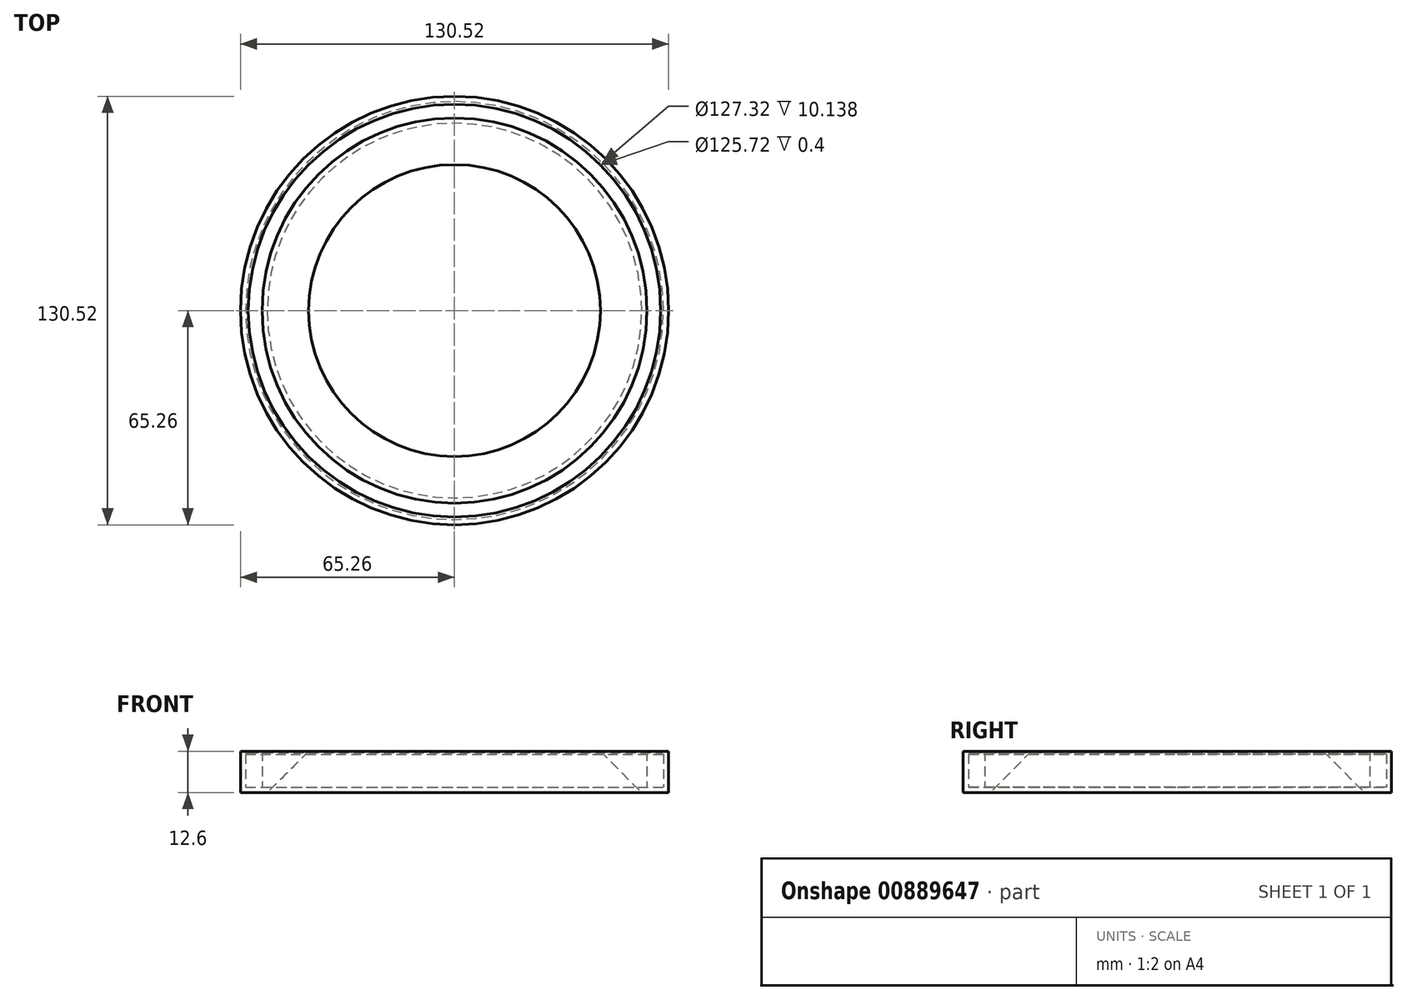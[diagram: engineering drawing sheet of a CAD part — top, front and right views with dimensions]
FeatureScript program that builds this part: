
annotation { "Feature Type Name" : "Feature", "Feature Type Description" : "" }
export const myFeature = defineFeature(function(context is Context, id is Id, definition is map)
    precondition{}
    {
        {
            var Q0;
            Q0=qCreatedBy(makeId("Front.planeOp"),FACE);
            var sketch = newSketch(context, id + "F0", { "sketchPlane" : qUnion([Q0])});
            skLineSegment(sketch, "E0", {"start": v(-65.26, 12.6) * mm, "end": v(-65.26, 0) * mm});
            skLineSegment(sketch, "E1", {"start": v(-65.26, 0) * mm, "end": v(-57.06, 0) * mm});
            skLineSegment(sketch, "E2", {"start": v(-57.06, 0) * mm, "end": v(-44.46, 12.6) * mm});
            skLineSegment(sketch, "E3", {"start": v(-44.46, 12.6) * mm, "end": v(-57.06, 12.6) * mm});
            skLineSegment(sketch, "E4", {"start": v(-57.06, 12.6) * mm, "end": v(-58.66, 12.6) * mm});
            skLineSegment(sketch, "E5", {"start": v(-58.66, 12.6) * mm, "end": v(-58.66, 1.6) * mm});
            skLineSegment(sketch, "E6", {"start": v(-58.66, 1.6) * mm, "end": v(-63.66, 1.6) * mm});
            skLineSegment(sketch, "E7", {"start": v(-63.66, 1.6) * mm, "end": v(-63.66, 12.6) * mm});
            skLineSegment(sketch, "E8", {"start": v(-63.66, 12.6) * mm, "end": v(-65.26, 12.6) * mm});
            skLineSegment(sketch, "E9", {"start": v(-63.66, 12.6) * mm, "end": v(-62.86, 12.6) * mm});
            skLineSegment(sketch, "E10", {"start": v(-62.86, 12.6) * mm, "end": v(-62.86, 12.2) * mm});
            skLineSegment(sketch, "E11", {"start": v(-62.86, 12.2) * mm, "end": v(-63.66, 11.74) * mm});
            skLineSegment(sketch, "E12", {"start": v(0, 0) * mm, "end": v(0, 31.7) * mm});
            skSolve(sketch);
        }
        {
            var Q0;
            Q0=makeQuery(id+"F0.imprint","IMPRINT",FACE,{"disambiguationData":[TD([[makeQuery(id+"F0.imprint","IMPRINT",EDGE,{"derivedFrom":sQuery(id+"F0.wireOp",EDGE,"E0")}),1.0]])]});
            var Q1;
            {var subQ0=sQuery(id+"F0.wireOp",EDGE,"E9");Q1=makeQuery(id+"F0.imprint","IMPRINT",FACE,{"disambiguationData":[TD([[makeQuery(id+"F0.imprint","IMPRINT",EDGE,{"derivedFrom":subQ0}),-1.0]])]});}
            var Q2;
            Q2=sQuery(id+"F0.wireOp",EDGE,"E12");
            revolve(context, id + "F1", {"surfaceOperationType" : NewSurfaceOperationType.NEW, "entities" : qUnion([Q0, Q1]), "axis" : qUnion([Q2]), "revolveType" : RevolveType.FULL});
        }
    });
